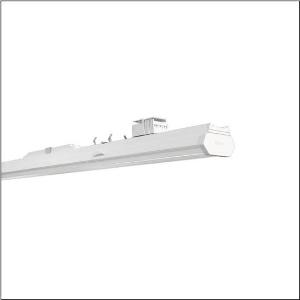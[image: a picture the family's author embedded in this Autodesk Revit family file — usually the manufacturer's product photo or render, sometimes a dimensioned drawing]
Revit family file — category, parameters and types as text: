
# Revit family: licross_r__11_protected_mo_51td1b7n48xg_edd2
name_source: partatom
category: Lighting Fixtures
units: mm (PartAtom-declared; Revit-internal decimal feet)

## family parameters
Cut with Voids When Loaded = No
Host = Face
Light Source = No
Part Type = Normal
Room Calculation Point = No
Round Connector Dimension = Use Diameter
Shared = No

## types (1)
- Licross® 11 Protected MO (1 x LED, 8190 lm, 48.6 W, 4000K)
    Apparent Load = 49 VA
    CIE Flux Codes = 54 82 95 97 100
    Color Rendering = 80
    Color Temperature = 4000K
    Default Elevation = 1800 mm
    Description = Licross® 11 Protected MO, luminaire insert, of sheet steel, galvanised, coil coated, white, length: 1.500mm, width: 90mm, height: 101mm, LED rated luminous flux: 8.190lm, light colour: 840, control gear: ON/OFF, with plug, 3-pole, with phase selection, mains connection: 220..240V, AC, 50/60Hz, rated input power: 49W, halogen-free wiring, primary optical cover: cover, of PMMA, light emission: direct distribution, primary light characteristic: symmetric, protection rating (complete): IP54, insulation class (complete): insulation class I (protective earthing), certification: CE, ENEC, VDE, UKCA, protection symbol: D if used in an environment with non-conductive dust loads with corresponding accessories, impact resistance: IK06, permissible ambient temperature for indoor applications: -25..+35°C, corresponds to IFS (International Featured Standards) requirements for safety and quality in the food industry, reducing of maximum allowable ambient temperature of 5°C with ceiling mounting, LABS conformity tested according to VDMA 24364:2018-05, packaging unit: 1 piece
    Height = 92 mm
    Lamp = 1 x LED
    Lamp Light Flux = 8190 lm
    Lamp Power = 48.6 W
    Lamp count = 1
    Length = 1500 mm
    Luminous efficacy = 169 lm/W
    Manufacturer = Siteco
    ModVariant = No
    Model = 51TD1B7N48XG
    Mounting Place = Ceiling
    Mounting Type = Pendant
    Number of Poles = 1
    OnlyDefault = Yes
    Power Factor = 1
    Product Name = Licross® 11 Protected MO
    Product group = luminaire insert
    ProductGroupID = 901
    Protection Class = Protection class I
    Protection Degree = IP 54
    RLX_Detail_Level = 1
    RLX_Emergency_Light_Flux = 0 lm
    RLX_Emergency_Type = 0
    RLX_Emergency_Type_DB = No
    RlxData = <blob elided: 20621 chars, md5=09d3bafc>
    Socket = socket
    Standby Power = 0 W
    System Light Flux = 8190 lm
    System Power = 49 W
    Type Comments = Product without accessories
    Type Image = l_1256145.jpg
    URL = http://relux.com
    VarID = ---
    Voltage = 0 V
    Weight = 0.00 kg
    Width = 88 mm

## geometry (parser evidence)
native form markers: Blend x4, Sweep x10
no freeform markers — native parametric forms only
